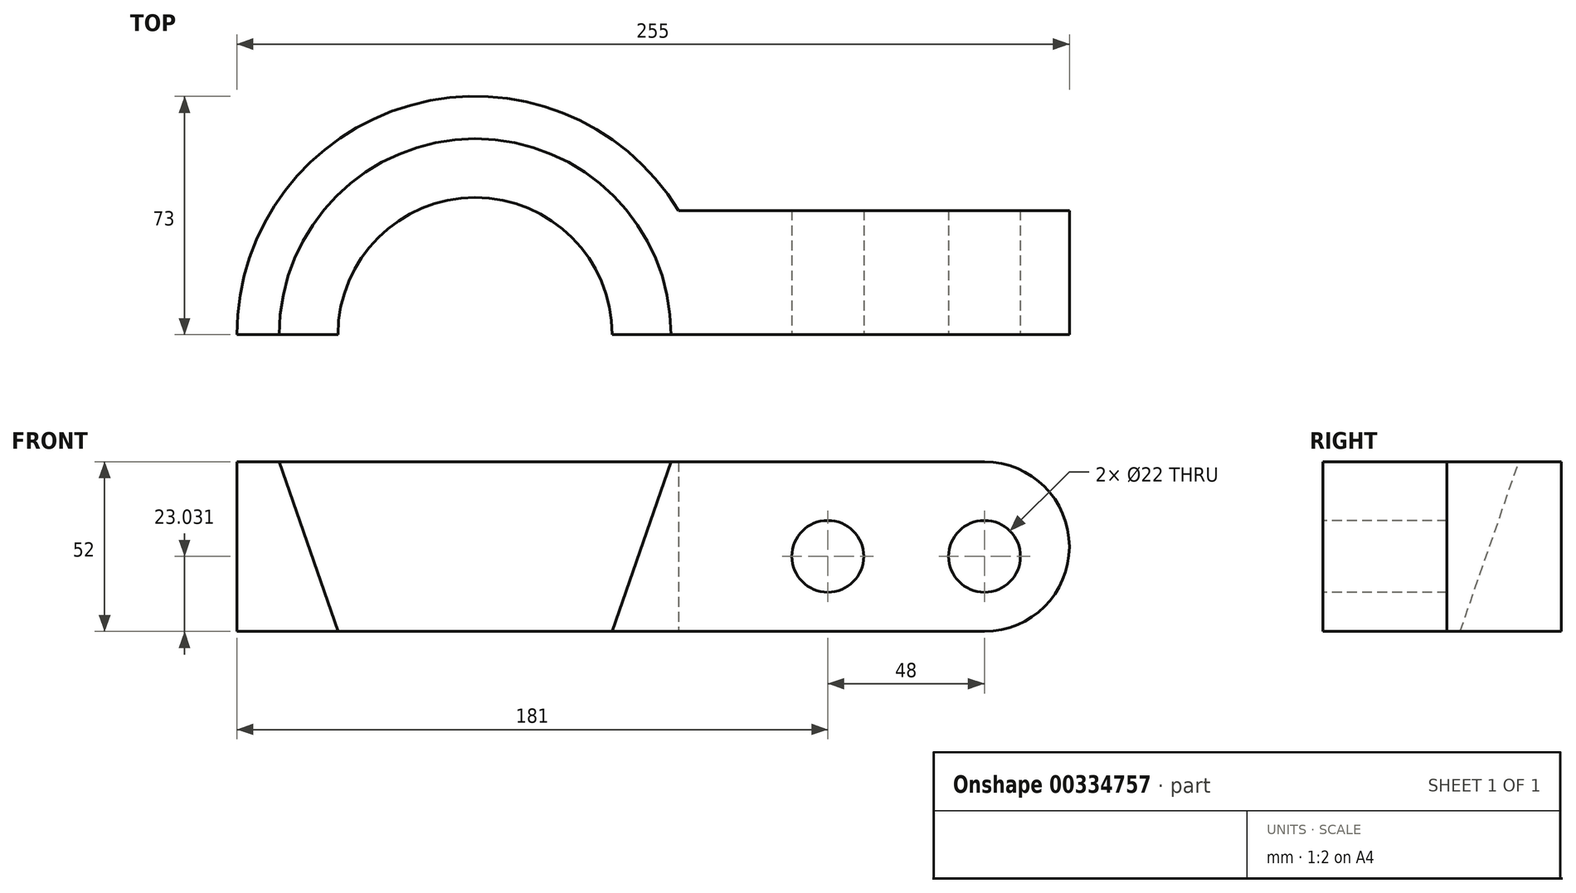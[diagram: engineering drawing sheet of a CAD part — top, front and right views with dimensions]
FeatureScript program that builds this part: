
annotation { "Feature Type Name" : "Feature", "Feature Type Description" : "" }
export const myFeature = defineFeature(function(context is Context, id is Id, definition is map)
    precondition{}
    {
        {
            var Q0;
            Q0=qCreatedBy(makeId("Top.planeOp"),FACE);
            var sketch = newSketch(context, id + "F0", { "sketchPlane" : qUnion([Q0])});
            skArc(sketch, "E0", {"start": v(42, 0) * mm, "mid": v(0, 42) * mm, "end": v(-42, 0) * mm});
            skArc(sketch, "E1", {"start": v(62.33, 38) * mm, "mid": v(-19.73, 70.28) * mm, "end": v(-73, 0) * mm});
            skLineSegment(sketch, "E2", {"start": v(-73, 0) * mm, "end": v(182, 0) * mm});
            skLineSegment(sketch, "E3", {"start": v(182, 0) * mm, "end": v(182, 38) * mm});
            skLineSegment(sketch, "E4", {"start": v(182, 38) * mm, "end": v(62.33, 38) * mm});
            skSolve(sketch);
        }
        {
            var Q0;
            {var subQ1=sQuery(id+"F0.wireOp",EDGE,"E0");Q0=makeQuery(id+"F0.imprint","IMPRINT",FACE,{"disambiguationData":[TD([[makeQuery(id+"F0.imprint","IMPRINT",EDGE,{"derivedFrom":subQ1}),-1.0]])]});}
            cPlane(context, id + "F1", {"entities" : qUnion([Q0]), "cplaneType" : CPlaneType.OFFSET, "offset" : 52 * mm, "width" : 150 * mm, "height" : 150 * mm});
        }
        {
            var Q0;
            Q0=qCreatedBy(id+"F1.planeOp",FACE);
            var sketch = newSketch(context, id + "F2", { "sketchPlane" : qUnion([Q0])});
            skArc(sketch, "E5", {"start": v(60, 0) * mm, "mid": v(0, 60) * mm, "end": v(-60, 0) * mm});
            skArc(sketch, "E6", {"start": v(62.33, 38) * mm, "mid": v(-19.73, 70.28) * mm, "end": v(-73, 0) * mm});
            skLineSegment(sketch, "E7", {"start": v(62.33, 38) * mm, "end": v(182, 38) * mm});
            skLineSegment(sketch, "E8", {"start": v(182, 38) * mm, "end": v(182, 0) * mm});
            skLineSegment(sketch, "E9", {"start": v(182, 0) * mm, "end": v(60, 0) * mm});
            skLineSegment(sketch, "E10.trimOffspring", {"start": v(-60, 0) * mm, "end": v(-73, 0) * mm});
            skSolve(sketch);
        }
        {
            var Q0;
            Q0=makeQuery(id+"F2.imprint","IMPRINT",FACE,{"disambiguationData":[TD([[makeQuery(id+"F2.imprint","IMPRINT",EDGE,{"derivedFrom":sQuery(id+"F2.wireOp",EDGE,"E5")}),-1.0]])]});
            var Q1;
            {var subQ1=sQuery(id+"F0.wireOp",EDGE,"E0");Q1=makeQuery(id+"F0.imprint","IMPRINT",FACE,{"disambiguationData":[TD([[makeQuery(id+"F0.imprint","IMPRINT",EDGE,{"derivedFrom":subQ1}),-1.0]])]});}
            loft(context, id + "F3", {"sheetProfilesArray" : [{ "sheetProfileEntities" : qUnion([Q0]) }, { "sheetProfileEntities" : qUnion([Q1]) }]});
        }
        {
            var Q0;
            Q0=makeQuery(id+"F3.opLoft","MID_CAP_EDGE",EDGE,{"disambiguationData":[OSD([sQuery(id+"F2.wireOp",EDGE,"E7"),sQuery(id+"F2.wireOp",EDGE,"E8"),sQuery(id+"F2.wireOp",EDGE,"E9")])],"capPos":0.0});
            var Q1;
            Q1=makeQuery(id+"F3.opLoft","MID_CAP_EDGE",EDGE,{"disambiguationData":[OSD([sQuery(id+"F0.wireOp",EDGE,"E2"),sQuery(id+"F0.wireOp",EDGE,"E3"),sQuery(id+"F0.wireOp",EDGE,"E4")])],"capPos":1.0});
            fillet(context, id + "F4", {"entities" : qUnion([Q0, Q1]), "radius" : 26 * mm, "tangentPropagation" : true, "allowEdgeOverflow" : false});
        }
        {
            var Q0;
            Q0=makeQuery(id+"F3.opLoft","SWEPT_FACE",FACE,{"disambiguationData":[OSD([sQuery(id+"F0.wireOp",EDGE,"E0"),sQuery(id+"F0.wireOp",EDGE,"E2"),sQuery(id+"F0.wireOp",EDGE,"E3"),sQuery(id+"F2.wireOp",EDGE,"E5"),sQuery(id+"F2.wireOp",EDGE,"E8"),sQuery(id+"F2.wireOp",EDGE,"E9")])]});
            var sketch = newSketch(context, id + "F5", { "sketchPlane" : qUnion([Q0])});
            skCircle(sketch, "E11", {"center": v(108, 23.03) * mm, "radius": 11 * mm});
            skCircle(sketch, "E12", {"center": v(156, 23.03) * mm, "radius": 11 * mm});
            skSolve(sketch);
        }
        {
            var Q0;
            Q0=makeQuery(id+"F5.imprint","IMPRINT",FACE,{"disambiguationData":[TD([[makeQuery(id+"F5.imprint","IMPRINT",EDGE,{"derivedFrom":sQuery(id+"F5.wireOp",EDGE,"E11")}),1.0]])]});
            var Q1;
            Q1=makeQuery(id+"F5.imprint","IMPRINT",FACE,{"disambiguationData":[TD([[makeQuery(id+"F5.imprint","IMPRINT",EDGE,{"derivedFrom":sQuery(id+"F5.wireOp",EDGE,"E12")}),1.0]])]});
            extrude(context, id + "F6", {"entities" : qUnion([Q0, Q1]), "operationType" : NewBodyOperationType.REMOVE, "endBound" : BoundingType.THROUGH_ALL, "oppositeDirection" : true, "depth" : 22 * mm});
        }
    });
